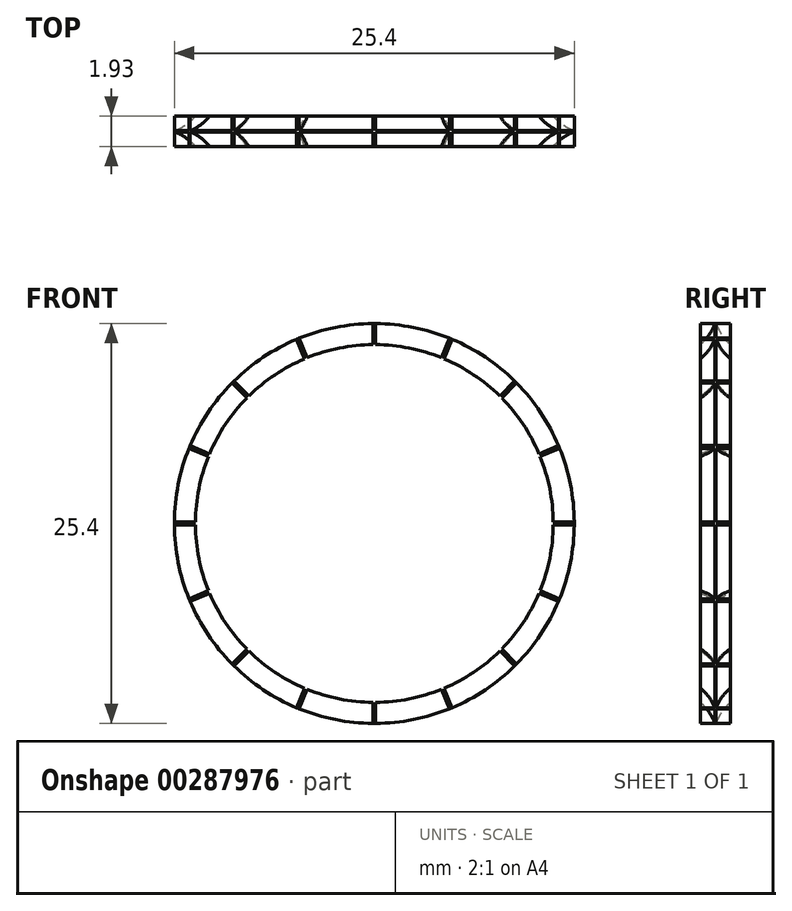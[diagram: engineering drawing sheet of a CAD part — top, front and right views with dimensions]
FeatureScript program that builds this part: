
annotation { "Feature Type Name" : "Feature", "Feature Type Description" : "" }
export const myFeature = defineFeature(function(context is Context, id is Id, definition is map)
    precondition{}
    {
        {
            var Q0;
            Q0=qCreatedBy(makeId("Front.planeOp"),FACE);
            var sketch = newSketch(context, id + "F0", { "sketchPlane" : qUnion([Q0])});
            skCircle(sketch, "E0", {"center": v(0, 0) * mm, "radius": 12.7 * mm});
            skSolve(sketch);
        }
        {
            var Q0;
            Q0 = qSketchRegion(id + "F0", true);
            extrude(context, id + "F1", {"entities" : qUnion([Q0]), "oppositeDirection" : true, "depth" : 1.93 * mm, "offsetDistance" : 25.4 * mm});
        }
        {
            var Q0;
            Q0=qCreatedBy(makeId("Right.planeOp"),FACE);
            var sketch = newSketch(context, id + "F2", { "sketchPlane" : qUnion([Q0])});
            skLineSegment(sketch, "E1", {"start": v(0.97, 0) * mm, "end": v(0.97, 14.02) * mm, "construction": true});
            skArc(sketch, "E2", {"start": v(0.97, 14.75) * mm, "mid": v(-5.23, 13.78) * mm, "end": v(0.97, 12.8) * mm});
            skArc(sketch, "E3", {"start": v(0.97, 12.8) * mm, "mid": v(7.16, 13.78) * mm, "end": v(0.97, 14.75) * mm});
            skLineSegment(sketch, "E4", {"start": v(-2.06, 13.78) * mm, "end": v(3.99, 13.78) * mm});
            skLineSegment(sketch, "E5", {"start": v(0, 0) * mm, "end": v(3.5, 0) * mm, "construction": true});
            skSolve(sketch);
        }
        {
            var Q0;
            Q0 = qSketchRegion(id + "F2", true);
            var Q1;
            Q1=sQuery(id+"F2.wireOp",EDGE,"E5");
            revolve(context, id + "F3", {"operationType" : NewBodyOperationType.REMOVE, "surfaceOperationType" : NewSurfaceOperationType.NEW, "entities" : qUnion([Q0]), "axis" : qUnion([Q1]), "revolveType" : RevolveType.FULL, "oppositeDirection" : true});
        }
        {
            var Q0;
            Q0=makeQuery(id+"F1.opExtrude","CAP_FACE",FACE,{"disambiguationData":[OSD([sQuery(id+"F0.wireOp",EDGE,"E0")])],"isStart":true});
            var sketch = newSketch(context, id + "F4", { "sketchPlane" : qUnion([Q0])});
            skLineSegment(sketch, "E6.bottom", {"start": v(-0.09, 13.2) * mm, "end": v(0.09, 13.2) * mm});
            skLineSegment(sketch, "E6.top", {"start": v(-0.09, 10.67) * mm, "end": v(0.09, 10.67) * mm});
            skLineSegment(sketch, "E6.left", {"start": v(-0.09, 13.2) * mm, "end": v(-0.09, 10.67) * mm});
            skLineSegment(sketch, "E6.right", {"start": v(0.09, 13.2) * mm, "end": v(0.09, 10.67) * mm});
            skLineSegment(sketch, "E7.1.0", {"start": v(5.14, 12.17) * mm, "end": v(4.16, 9.82) * mm});
            skLineSegment(sketch, "E7.1.1", {"start": v(4.97, 12.24) * mm, "end": v(4, 9.89) * mm});
            skLineSegment(sketch, "E7.1.2", {"start": v(4, 9.89) * mm, "end": v(4.16, 9.82) * mm});
            skLineSegment(sketch, "E7.1.3", {"start": v(4.97, 12.24) * mm, "end": v(5.14, 12.17) * mm});
            skLineSegment(sketch, "E7.2.0", {"start": v(9.4, 9.28) * mm, "end": v(7.6, 7.48) * mm});
            skLineSegment(sketch, "E7.2.1", {"start": v(9.28, 9.4) * mm, "end": v(7.48, 7.6) * mm});
            skLineSegment(sketch, "E7.2.2", {"start": v(7.48, 7.6) * mm, "end": v(7.6, 7.48) * mm});
            skLineSegment(sketch, "E7.2.3", {"start": v(9.28, 9.4) * mm, "end": v(9.4, 9.28) * mm});
            skLineSegment(sketch, "E7.3.0", {"start": v(12.24, 4.97) * mm, "end": v(9.89, 4) * mm});
            skLineSegment(sketch, "E7.3.1", {"start": v(12.17, 5.14) * mm, "end": v(9.82, 4.16) * mm});
            skLineSegment(sketch, "E7.3.2", {"start": v(9.82, 4.16) * mm, "end": v(9.89, 4) * mm});
            skLineSegment(sketch, "E7.3.3", {"start": v(12.17, 5.14) * mm, "end": v(12.24, 4.97) * mm});
            skLineSegment(sketch, "E7.4.0", {"start": v(13.2, -0.09) * mm, "end": v(10.67, -0.09) * mm});
            skLineSegment(sketch, "E7.4.1", {"start": v(13.2, 0.09) * mm, "end": v(10.67, 0.09) * mm});
            skLineSegment(sketch, "E7.4.2", {"start": v(10.67, 0.09) * mm, "end": v(10.67, -0.09) * mm});
            skLineSegment(sketch, "E7.4.3", {"start": v(13.2, 0.09) * mm, "end": v(13.2, -0.09) * mm});
            skLineSegment(sketch, "E7.5.0", {"start": v(12.17, -5.14) * mm, "end": v(9.82, -4.16) * mm});
            skLineSegment(sketch, "E7.5.1", {"start": v(12.24, -4.97) * mm, "end": v(9.89, -4) * mm});
            skLineSegment(sketch, "E7.5.2", {"start": v(9.89, -4) * mm, "end": v(9.82, -4.16) * mm});
            skLineSegment(sketch, "E7.5.3", {"start": v(12.24, -4.97) * mm, "end": v(12.17, -5.14) * mm});
            skLineSegment(sketch, "E7.6.0", {"start": v(9.28, -9.4) * mm, "end": v(7.48, -7.6) * mm});
            skLineSegment(sketch, "E7.6.1", {"start": v(9.4, -9.28) * mm, "end": v(7.6, -7.48) * mm});
            skLineSegment(sketch, "E7.6.2", {"start": v(7.6, -7.48) * mm, "end": v(7.48, -7.6) * mm});
            skLineSegment(sketch, "E7.6.3", {"start": v(9.4, -9.28) * mm, "end": v(9.28, -9.4) * mm});
            skLineSegment(sketch, "E7.7.0", {"start": v(4.97, -12.24) * mm, "end": v(4, -9.89) * mm});
            skLineSegment(sketch, "E7.7.1", {"start": v(5.14, -12.17) * mm, "end": v(4.16, -9.82) * mm});
            skLineSegment(sketch, "E7.7.2", {"start": v(4.16, -9.82) * mm, "end": v(4, -9.89) * mm});
            skLineSegment(sketch, "E7.7.3", {"start": v(5.14, -12.17) * mm, "end": v(4.97, -12.24) * mm});
            skLineSegment(sketch, "E7.8.0", {"start": v(-0.09, -13.2) * mm, "end": v(-0.09, -10.67) * mm});
            skLineSegment(sketch, "E7.8.1", {"start": v(0.09, -13.2) * mm, "end": v(0.09, -10.67) * mm});
            skLineSegment(sketch, "E7.8.2", {"start": v(0.09, -10.67) * mm, "end": v(-0.09, -10.67) * mm});
            skLineSegment(sketch, "E7.8.3", {"start": v(0.09, -13.2) * mm, "end": v(-0.09, -13.2) * mm});
            skPoint(sketch, "E7.center", {"position": v(0, 0) * mm});
            skLineSegment(sketch, "E7.anchor1", {"start": v(0, 0) * mm, "end": v(-0.09, 10.67) * mm, "construction": true});
            skLineSegment(sketch, "E7.anchor2", {"start": v(0, 0) * mm, "end": v(-0.09, 10.67) * mm, "construction": true});
            skLineSegment(sketch, "E8.3.9.0", {"start": v(-4.97, -12.24) * mm, "end": v(-4, -9.89) * mm});
            skLineSegment(sketch, "E8.5.9.0", {"start": v(-5.14, -12.17) * mm, "end": v(-4.16, -9.82) * mm});
            skLineSegment(sketch, "E8.6.9.0", {"start": v(-4, -9.89) * mm, "end": v(-4.16, -9.82) * mm});
            skLineSegment(sketch, "E8.9.9.0", {"start": v(-4.97, -12.24) * mm, "end": v(-5.14, -12.17) * mm});
            skLineSegment(sketch, "E8.3.10.0", {"start": v(-9.28, -9.4) * mm, "end": v(-7.48, -7.6) * mm});
            skLineSegment(sketch, "E8.5.10.0", {"start": v(-9.4, -9.28) * mm, "end": v(-7.6, -7.48) * mm});
            skLineSegment(sketch, "E8.6.10.0", {"start": v(-7.48, -7.6) * mm, "end": v(-7.6, -7.48) * mm});
            skLineSegment(sketch, "E8.9.10.0", {"start": v(-9.28, -9.4) * mm, "end": v(-9.4, -9.28) * mm});
            skLineSegment(sketch, "E8.3.11.0", {"start": v(-12.17, -5.14) * mm, "end": v(-9.82, -4.16) * mm});
            skLineSegment(sketch, "E8.5.11.0", {"start": v(-12.24, -4.97) * mm, "end": v(-9.89, -4) * mm});
            skLineSegment(sketch, "E8.6.11.0", {"start": v(-9.82, -4.16) * mm, "end": v(-9.89, -4) * mm});
            skLineSegment(sketch, "E8.9.11.0", {"start": v(-12.17, -5.14) * mm, "end": v(-12.24, -4.97) * mm});
            skLineSegment(sketch, "E8.3.12.0", {"start": v(-13.2, -0.09) * mm, "end": v(-10.67, -0.09) * mm});
            skLineSegment(sketch, "E8.5.12.0", {"start": v(-13.2, 0.09) * mm, "end": v(-10.67, 0.09) * mm});
            skLineSegment(sketch, "E8.6.12.0", {"start": v(-10.67, -0.09) * mm, "end": v(-10.67, 0.09) * mm});
            skLineSegment(sketch, "E8.9.12.0", {"start": v(-13.2, -0.09) * mm, "end": v(-13.2, 0.09) * mm});
            skLineSegment(sketch, "E8.3.13.0", {"start": v(-12.24, 4.97) * mm, "end": v(-9.89, 4) * mm});
            skLineSegment(sketch, "E8.5.13.0", {"start": v(-12.17, 5.14) * mm, "end": v(-9.82, 4.16) * mm});
            skLineSegment(sketch, "E8.6.13.0", {"start": v(-9.89, 4) * mm, "end": v(-9.82, 4.16) * mm});
            skLineSegment(sketch, "E8.9.13.0", {"start": v(-12.24, 4.97) * mm, "end": v(-12.17, 5.14) * mm});
            skLineSegment(sketch, "E8.3.14.0", {"start": v(-9.4, 9.28) * mm, "end": v(-7.6, 7.48) * mm});
            skLineSegment(sketch, "E8.5.14.0", {"start": v(-9.28, 9.4) * mm, "end": v(-7.48, 7.6) * mm});
            skLineSegment(sketch, "E8.6.14.0", {"start": v(-7.6, 7.48) * mm, "end": v(-7.48, 7.6) * mm});
            skLineSegment(sketch, "E8.9.14.0", {"start": v(-9.4, 9.28) * mm, "end": v(-9.28, 9.4) * mm});
            skLineSegment(sketch, "E8.3.15.0", {"start": v(-5.14, 12.17) * mm, "end": v(-4.16, 9.82) * mm});
            skLineSegment(sketch, "E8.5.15.0", {"start": v(-4.97, 12.24) * mm, "end": v(-4, 9.89) * mm});
            skLineSegment(sketch, "E8.6.15.0", {"start": v(-4.16, 9.82) * mm, "end": v(-4, 9.89) * mm});
            skLineSegment(sketch, "E8.9.15.0", {"start": v(-5.14, 12.17) * mm, "end": v(-4.97, 12.24) * mm});
            skSolve(sketch);
        }
        {
            var Q0;
            Q0 = qSketchRegion(id + "F4", true);
            extrude(context, id + "F5", {"entities" : qUnion([Q0]), "operationType" : NewBodyOperationType.ADD, "oppositeDirection" : true, "depth" : 1.93 * mm, "offsetDistance" : 25.4 * mm});
        }
        {
            var Q0;
            Q0=makeQuery(id+"F5.boolean.opBoolean","MERGE",FACE,{"derivedFrom":[makeQuery(id+"F1.opExtrude","CAP_FACE",FACE,{"disambiguationData":[OSD([sQuery(id+"F0.wireOp",EDGE,"E0")])],"isStart":true}),makeQuery(id+"F5.opExtrude","CAP_FACE",FACE,{"disambiguationData":[OSD([sQuery(id+"F4.wireOp",EDGE,"E7.1.0"),sQuery(id+"F4.wireOp",EDGE,"E7.1.1"),sQuery(id+"F4.wireOp",EDGE,"E7.1.2"),sQuery(id+"F4.wireOp",EDGE,"E7.1.3")])],"isStart":true}),makeQuery(id+"F5.opExtrude","CAP_FACE",FACE,{"disambiguationData":[OSD([sQuery(id+"F4.wireOp",EDGE,"E7.2.0"),sQuery(id+"F4.wireOp",EDGE,"E7.2.1"),sQuery(id+"F4.wireOp",EDGE,"E7.2.2"),sQuery(id+"F4.wireOp",EDGE,"E7.2.3")])],"isStart":true}),makeQuery(id+"F5.opExtrude","CAP_FACE",FACE,{"disambiguationData":[OSD([sQuery(id+"F4.wireOp",EDGE,"E7.3.0"),sQuery(id+"F4.wireOp",EDGE,"E7.3.1"),sQuery(id+"F4.wireOp",EDGE,"E7.3.2"),sQuery(id+"F4.wireOp",EDGE,"E7.3.3")])],"isStart":true}),makeQuery(id+"F5.opExtrude","CAP_FACE",FACE,{"disambiguationData":[OSD([sQuery(id+"F4.wireOp",EDGE,"E7.4.0"),sQuery(id+"F4.wireOp",EDGE,"E7.4.1"),sQuery(id+"F4.wireOp",EDGE,"E7.4.2"),sQuery(id+"F4.wireOp",EDGE,"E7.4.3")])],"isStart":true}),makeQuery(id+"F5.opExtrude","CAP_FACE",FACE,{"disambiguationData":[OSD([sQuery(id+"F4.wireOp",EDGE,"E7.5.0"),sQuery(id+"F4.wireOp",EDGE,"E7.5.1"),sQuery(id+"F4.wireOp",EDGE,"E7.5.2"),sQuery(id+"F4.wireOp",EDGE,"E7.5.3")])],"isStart":true}),makeQuery(id+"F5.opExtrude","CAP_FACE",FACE,{"disambiguationData":[OSD([sQuery(id+"F4.wireOp",EDGE,"E7.6.0"),sQuery(id+"F4.wireOp",EDGE,"E7.6.1"),sQuery(id+"F4.wireOp",EDGE,"E7.6.2"),sQuery(id+"F4.wireOp",EDGE,"E7.6.3")])],"isStart":true}),makeQuery(id+"F5.opExtrude","CAP_FACE",FACE,{"disambiguationData":[OSD([sQuery(id+"F4.wireOp",EDGE,"E7.7.0"),sQuery(id+"F4.wireOp",EDGE,"E7.7.1"),sQuery(id+"F4.wireOp",EDGE,"E7.7.2"),sQuery(id+"F4.wireOp",EDGE,"E7.7.3")])],"isStart":true}),makeQuery(id+"F5.opExtrude","CAP_FACE",FACE,{"disambiguationData":[OSD([sQuery(id+"F4.wireOp",EDGE,"E7.8.0"),sQuery(id+"F4.wireOp",EDGE,"E7.8.1"),sQuery(id+"F4.wireOp",EDGE,"E7.8.2"),sQuery(id+"F4.wireOp",EDGE,"E7.8.3")])],"isStart":true}),makeQuery(id+"F5.opExtrude","CAP_FACE",FACE,{"disambiguationData":[OSD([sQuery(id+"F4.wireOp",EDGE,"E7.9.0"),sQuery(id+"F4.wireOp",EDGE,"E7.9.1"),sQuery(id+"F4.wireOp",EDGE,"E7.9.2"),sQuery(id+"F4.wireOp",EDGE,"E7.9.3")])],"isStart":true}),makeQuery(id+"F5.opExtrude","CAP_FACE",FACE,{"disambiguationData":[OSD([sQuery(id+"F4.wireOp",EDGE,"E7.10.0"),sQuery(id+"F4.wireOp",EDGE,"E7.10.1"),sQuery(id+"F4.wireOp",EDGE,"E7.10.2"),sQuery(id+"F4.wireOp",EDGE,"E7.10.3")])],"isStart":true}),makeQuery(id+"F5.opExtrude","CAP_FACE",FACE,{"disambiguationData":[OSD([sQuery(id+"F4.wireOp",EDGE,"E7.11.0"),sQuery(id+"F4.wireOp",EDGE,"E7.11.1"),sQuery(id+"F4.wireOp",EDGE,"E7.11.2"),sQuery(id+"F4.wireOp",EDGE,"E7.11.3")])],"isStart":true}),makeQuery(id+"F5.opExtrude","CAP_FACE",FACE,{"disambiguationData":[OSD([sQuery(id+"F4.wireOp",EDGE,"E7.12.0"),sQuery(id+"F4.wireOp",EDGE,"E7.12.1"),sQuery(id+"F4.wireOp",EDGE,"E7.12.2"),sQuery(id+"F4.wireOp",EDGE,"E7.12.3")])],"isStart":true}),makeQuery(id+"F5.opExtrude","CAP_FACE",FACE,{"disambiguationData":[OSD([sQuery(id+"F4.wireOp",EDGE,"E7.13.0"),sQuery(id+"F4.wireOp",EDGE,"E7.13.1"),sQuery(id+"F4.wireOp",EDGE,"E7.13.2"),sQuery(id+"F4.wireOp",EDGE,"E7.13.3")])],"isStart":true}),makeQuery(id+"F5.opExtrude","CAP_FACE",FACE,{"disambiguationData":[OSD([sQuery(id+"F4.wireOp",EDGE,"E7.14.0"),sQuery(id+"F4.wireOp",EDGE,"E7.14.1"),sQuery(id+"F4.wireOp",EDGE,"E7.14.2"),sQuery(id+"F4.wireOp",EDGE,"E7.14.3")])],"isStart":true}),makeQuery(id+"F5.opExtrude","CAP_FACE",FACE,{"disambiguationData":[OSD([sQuery(id+"F4.wireOp",EDGE,"E7.15.0"),sQuery(id+"F4.wireOp",EDGE,"E7.15.1"),sQuery(id+"F4.wireOp",EDGE,"E7.15.2"),sQuery(id+"F4.wireOp",EDGE,"E7.15.3")])],"isStart":true}),makeQuery(id+"F5.opExtrude","CAP_FACE",FACE,{"disambiguationData":[OSD([sQuery(id+"F4.wireOp",EDGE,"E7.16.0"),sQuery(id+"F4.wireOp",EDGE,"E7.16.1"),sQuery(id+"F4.wireOp",EDGE,"E7.16.2"),sQuery(id+"F4.wireOp",EDGE,"E7.16.3")])],"isStart":true}),makeQuery(id+"F5.opExtrude","CAP_FACE",FACE,{"disambiguationData":[OSD([sQuery(id+"F4.wireOp",EDGE,"E7.17.0"),sQuery(id+"F4.wireOp",EDGE,"E7.17.1"),sQuery(id+"F4.wireOp",EDGE,"E7.17.2"),sQuery(id+"F4.wireOp",EDGE,"E7.17.3")])],"isStart":true}),makeQuery(id+"F5.opExtrude","CAP_FACE",FACE,{"disambiguationData":[OSD([sQuery(id+"F4.wireOp",EDGE,"E7.18.0"),sQuery(id+"F4.wireOp",EDGE,"E7.18.1"),sQuery(id+"F4.wireOp",EDGE,"E7.18.2"),sQuery(id+"F4.wireOp",EDGE,"E7.18.3")])],"isStart":true}),makeQuery(id+"F5.opExtrude","CAP_FACE",FACE,{"disambiguationData":[OSD([sQuery(id+"F4.wireOp",EDGE,"E7.19.0"),sQuery(id+"F4.wireOp",EDGE,"E7.19.1"),sQuery(id+"F4.wireOp",EDGE,"E7.19.2"),sQuery(id+"F4.wireOp",EDGE,"E7.19.3")])],"isStart":true}),makeQuery(id+"F5.opExtrude","CAP_FACE",FACE,{"disambiguationData":[OSD([sQuery(id+"F4.wireOp",EDGE,"E7.20.0"),sQuery(id+"F4.wireOp",EDGE,"E7.20.1"),sQuery(id+"F4.wireOp",EDGE,"E7.20.2"),sQuery(id+"F4.wireOp",EDGE,"E7.20.3")])],"isStart":true}),makeQuery(id+"F5.opExtrude","CAP_FACE",FACE,{"disambiguationData":[OSD([sQuery(id+"F4.wireOp",EDGE,"E7.21.0"),sQuery(id+"F4.wireOp",EDGE,"E7.21.1"),sQuery(id+"F4.wireOp",EDGE,"E7.21.2"),sQuery(id+"F4.wireOp",EDGE,"E7.21.3")])],"isStart":true}),makeQuery(id+"F5.opExtrude","CAP_FACE",FACE,{"disambiguationData":[OSD([sQuery(id+"F4.wireOp",EDGE,"E7.22.0"),sQuery(id+"F4.wireOp",EDGE,"E7.22.1"),sQuery(id+"F4.wireOp",EDGE,"E7.22.2"),sQuery(id+"F4.wireOp",EDGE,"E7.22.3")])],"isStart":true})]});
            var sketch = newSketch(context, id + "F6", { "sketchPlane" : qUnion([Q0])});
            skCircle(sketch, "E9", {"center": v(0, 0) * mm, "radius": 12.7 * mm});
            skCircle(sketch, "E10", {"center": v(0, 0) * mm, "radius": 13.97 * mm});
            skSolve(sketch);
        }
        {
            var Q0;
            Q0 = qSketchRegion(id + "F6", true);
            extrude(context, id + "F7", {"entities" : qUnion([Q0]), "operationType" : NewBodyOperationType.REMOVE, "oppositeDirection" : true, "depth" : 25.4 * mm, "offsetDistance" : 25.4 * mm});
        }
    });
